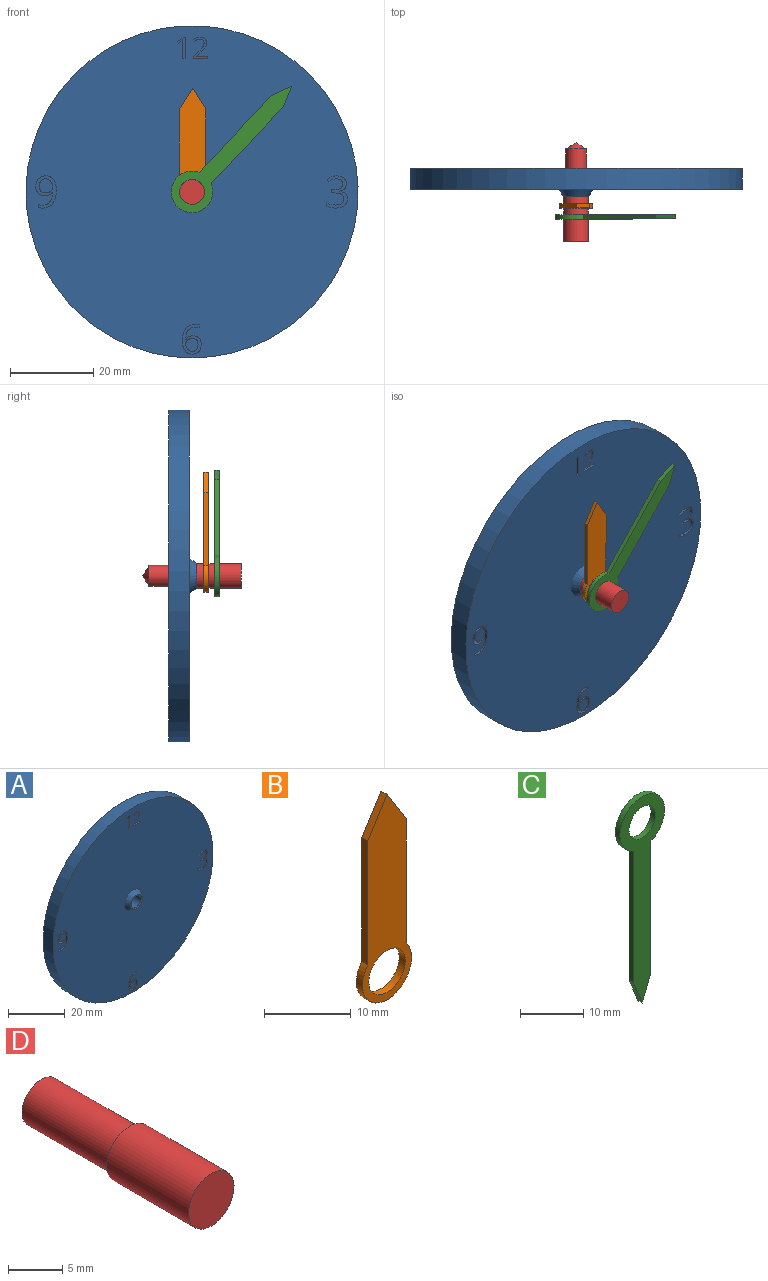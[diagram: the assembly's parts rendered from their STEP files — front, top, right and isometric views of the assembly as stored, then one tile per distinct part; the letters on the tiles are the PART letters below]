
ASSEMBLY  parts=4 mates=4
PART A: 121 faces, bbox 80x6.8x80 mm
  f0: plane 80x80mm, normal (0,-1,0), area 4903.6mm2, adj f1,f2,f6,f7,f8,f9,f10,f11
  f1: cone r=4.25mm half-angle=35.4deg, axis (0,1,0), area 50.1mm2, adj f0,f5
  f2: cylinder r=40mm len=80mm, axis (0,1,0), area 1256.6mm2, adj f0,f3
  f3: plane 80x80mm, normal (0,1,0), area 5006.9mm2, adj f2,f4
  f4: cylinder r=2.5mm len=6.53mm, axis (0,-1,0), area 102.5mm2, adj f3,f5
  f5: cone r=2.5mm half-angle=60deg, axis (0,-1,0), area 9.3mm2, adj f1,f4
  f6: extruded ~2.25x1.5mm, area 3.6mm2, adj f0,f7,f30,f31
  f7: extruded ~1.71x1.5mm, area 2.9mm2, adj f0,f6,f8,f31
  f8: extruded ~1.6x1.5mm, area 2.6mm2, adj f0,f7,f9,f31
  f9: extruded ~1.7x1.5mm, area 2.8mm2, adj f0,f8,f10,f31
  f10: extruded ~1.53x1.5mm, area 2.5mm2, adj f0,f9,f11,f31
  f11: extruded ~1.5x1.47mm, area 2.4mm2, adj f0,f10,f12,f31
  f12: extruded ~1.65x1.5mm, area 2.9mm2, adj f0,f11,f13,f31
  f13: plane 1.5x0.06mm, normal (0,0,-1), area 0.1mm2, adj f0,f12,f14,f31
  f14: extruded ~2.19x1.5mm, area 3.5mm2, adj f0,f13,f15,f31
  f15: extruded ~1.71x1.5mm, area 2.9mm2, adj f0,f14,f16,f31
  f16: extruded ~1.5x0.84mm, area 1.3mm2, adj f0,f15,f17,f31
  f17: plane 1.5x0.68mm, normal (-1,0,0), area 1mm2, adj f0,f16,f18,f31
  f18: extruded ~1.5x0.84mm, area 1.3mm2, adj f0,f17,f19,f31
  f19: extruded ~2.35x1.5mm, area 4mm2, adj f0,f18,f30,f31
  f20: extruded ~1.5x0.8mm, area 1.3mm2, adj f21,f29,f31,f32
  f21: extruded ~1.5x0.67mm, area 1.3mm2, adj f20,f22,f31,f32
  f22: extruded ~1.5x0.91mm, area 1.4mm2, adj f21,f23,f31,f32
  f23: extruded ~1.5x0.64mm, area 1mm2, adj f22,f24,f31,f32
  f24: extruded ~1.5x0.57mm, area 1.1mm2, adj f23,f25,f31,f32
  f25: extruded ~1.5x0.78mm, area 1.2mm2, adj f24,f26,f31,f32
  f26: extruded ~1.5x1.03mm, area 1.7mm2, adj f25,f27,f31,f32
  f27: extruded ~1.5x1.08mm, area 1.7mm2, adj f26,f28,f31,f32
  f28: extruded ~1.5x1.23mm, area 2mm2, adj f27,f29,f31,f32
  f29: extruded ~1.5x1.05mm, area 1.8mm2, adj f20,f28,f31,f32
  f30: extruded ~3.06x1.5mm, area 4.8mm2, adj f0,f6,f19,f31
  f31: plane 7.14x4.53mm, normal (0,-1,0), area 12.5mm2, adj f6,f7,f8,f9,f10,f11,f12,f13
  f32: plane 3.13x2.94mm, normal (0,-1,0), area 7.4mm2, adj f20,f21,f22,f23,f24,f25,f26,f27
  f33: extruded ~1.5x1.38mm, area 2.3mm2, adj f0,f34,f60,f61
  f34: extruded ~1.71x1.5mm, area 2.7mm2, adj f0,f33,f35,f61
  f35: extruded ~1.5x1.28mm, area 1.9mm2, adj f0,f34,f36,f61
  f36: extruded ~1.5x1.07mm, area 1.8mm2, adj f0,f35,f37,f61
  f37: plane 1.5x0.58mm, normal (0.8,0,0.6), area 1.1mm2, adj f0,f36,f38,f61
  f38: extruded ~1.5x1mm, area 1.7mm2, adj f0,f37,f39,f61
  f39: extruded ~1.5x0.93mm, area 1.4mm2, adj f0,f38,f40,f61
  f40: extruded ~1.5x1.03mm, area 1.6mm2, adj f0,f39,f41,f61
  f41: extruded ~1.5x0.87mm, area 1.5mm2, adj f0,f40,f42,f61
  f42: extruded ~1.5x1.08mm, area 1.9mm2, adj f0,f41,f43,f61
  f43: extruded ~1.5x1.4mm, area 2.2mm2, adj f0,f42,f44,f61
  f44: plane 1.5x0.75mm, normal (0,0,-1), area 1.1mm2, adj f0,f43,f45,f61
  f45: plane 1.5x0.74mm, normal (1,0,0), area 1.1mm2, adj f0,f44,f46,f61
  f46: plane 1.5x0.74mm, normal (0,0,1), area 1.1mm2, adj f0,f45,f47,f61
  f47: extruded ~2.15x1.5mm, area 4.3mm2, adj f0,f46,f48,f61
  f48: extruded ~1.95x1.53mm, area 4.3mm2, adj f0,f47,f49,f61
  f49: extruded ~1.5x1.05mm, area 1.6mm2, adj f0,f48,f50,f61
  f50: extruded ~1.5x1.04mm, area 1.7mm2, adj f0,f49,f51,f61
  f51: plane 1.5x0.81mm, normal (1,0,0), area 1.2mm2, adj f0,f50,f52,f61
  f52: extruded ~1.5x0.97mm, area 1.5mm2, adj f0,f51,f53,f61
  f53: extruded ~1.5x1.1mm, area 1.7mm2, adj f0,f52,f54,f61
  f54: extruded ~2.12x1.5mm, area 3.4mm2, adj f0,f53,f55,f61
  f55: extruded ~1.66x1.5mm, area 2.8mm2, adj f0,f54,f56,f61
  f56: extruded ~1.5x1.22mm, area 2mm2, adj f0,f55,f57,f61
  f57: extruded ~1.5x1.35mm, area 2.2mm2, adj f0,f56,f58,f61
  f58: plane 1.5x0.04mm, normal (-1,0,0), area 0.1mm2, adj f0,f57,f59,f61
  f59: extruded ~1.5x1.15mm, area 2mm2, adj f0,f58,f60,f61
  f60: extruded ~1.5x1.18mm, area 1.9mm2, adj f0,f33,f59,f61
  f61: plane 7.75x4.93mm, normal (0,-1,0), area 13.2mm2, adj f33,f34,f35,f36,f37,f38,f39,f40
  f62: plane 1.5x0.55mm, normal (-1,0,0), area 0.8mm2, adj f0,f63,f81,f82
  f63: plane 2.67x1.5mm, normal (0,0,-1), area 4mm2, adj f0,f62,f64,f82
  f64: plane 1.5x0.03mm, normal (-1,0,0), area 0mm2, adj f0,f63,f65,f82
  f65: plane 1.5x1.14mm, normal (-0.7,0,0.71), area 2.4mm2, adj f0,f64,f66,f82
  f66: extruded ~1.5x1.22mm, area 2.4mm2, adj f0,f65,f67,f82
  f67: extruded ~1.5x0.98mm, area 1.5mm2, adj f0,f66,f68,f82
  f68: extruded ~1.5x1.01mm, area 1.7mm2, adj f0,f67,f69,f82
  f69: extruded ~1.5x1.15mm, area 1.9mm2, adj f0,f68,f70,f82
  f70: extruded ~1.56x1.5mm, area 2.6mm2, adj f0,f69,f71,f82
  f71: plane 1.5x0.4mm, normal (0.79,0,0.61), area 0.8mm2, adj f0,f70,f72,f82
  f72: extruded ~1.5x0.64mm, area 1.1mm2, adj f0,f71,f73,f82
  f73: extruded ~1.5x0.61mm, area 0.9mm2, adj f0,f72,f74,f82
  f74: extruded ~1.5x0.7mm, area 1.1mm2, adj f0,f73,f75,f82
  f75: extruded ~1.5x0.66mm, area 1.1mm2, adj f0,f74,f76,f82
  f76: extruded ~1.5x0.55mm, area 0.8mm2, adj f0,f75,f77,f82
  f77: extruded ~1.5x0.53mm, area 0.9mm2, adj f0,f76,f78,f82
  f78: extruded ~1.5x0.9mm, area 1.8mm2, adj f0,f77,f79,f82
  f79: plane 1.5x1.37mm, normal (0.71,0,-0.71), area 2.9mm2, adj f0,f78,f80,f82
  f80: plane 1.5x0.51mm, normal (1,0,0), area 0.8mm2, adj f0,f79,f81,f82
  f81: plane 3.41x1.5mm, normal (0,0,1), area 5.1mm2, adj f0,f62,f80,f82
  f82: plane 5.27x3.41mm, normal (0,-1,0), area 5.9mm2, adj f62,f63,f64,f65,f66,f67,f68,f69
  f83: plane 5.19x1.5mm, normal (-1,0,0), area 7.8mm2, adj f0,f84,f91,f92
  f84: plane 1.5x0.5mm, normal (0,0,-1), area 0.7mm2, adj f0,f83,f85,f92
  f85: plane 1.5x1.37mm, normal (0.61,0,-0.79), area 2.6mm2, adj f0,f84,f86,f92
  f86: plane 1.5x0.4mm, normal (0.79,0,0.61), area 0.8mm2, adj f0,f85,f87,f92
  f87: extruded ~1.5x0.85mm, area 1.6mm2, adj f0,f86,f88,f92
  f88: extruded ~1.5x0.17mm, area 0.3mm2, adj f0,f87,f89,f92
  f89: extruded ~1.5x0.87mm, area 1.3mm2, adj f0,f88,f90,f92
  f90: plane 3.7x1.5mm, normal (1,0,0), area 5.6mm2, adj f0,f89,f91,f92
  f91: plane 1.5x0.58mm, normal (0,0,1), area 0.9mm2, adj f0,f83,f90,f92
  f92: plane 5.19x1.87mm, normal (0,-1,0), area 3.7mm2, adj f83,f84,f85,f86,f87,f88,f89,f90
  f93: extruded ~1.78x1.5mm, area 2.7mm2, adj f0,f94,f118,f119
  f94: extruded ~1.5x1.15mm, area 2.2mm2, adj f0,f93,f95,f119
  f95: extruded ~1.5x1.34mm, area 2.1mm2, adj f0,f94,f96,f119
  f96: extruded ~1.73x1.5mm, area 2.9mm2, adj f0,f95,f97,f119
  f97: extruded ~1.85x1.5mm, area 3mm2, adj f0,f96,f98,f119
  f98: extruded ~1.67x1.5mm, area 2.7mm2, adj f0,f97,f99,f119
  f99: extruded ~1.59x1.5mm, area 2.6mm2, adj f0,f98,f100,f119
  f100: extruded ~1.5x1.06mm, area 1.6mm2, adj f0,f99,f101,f119
  f101: extruded ~1.5x0.75mm, area 1.5mm2, adj f0,f100,f102,f119
  f102: plane 1.5x0.06mm, normal (0,0,1), area 0.1mm2, adj f0,f101,f103,f119
  f103: extruded ~2.35x1.5mm, area 3.7mm2, adj f0,f102,f104,f119
  f104: extruded ~1.87x1.5mm, area 3.1mm2, adj f0,f103,f105,f119
  f105: extruded ~1.5x0.94mm, area 1.4mm2, adj f0,f104,f106,f119
  f106: plane 1.5x0.74mm, normal (1,0,0), area 1.1mm2, adj f0,f105,f107,f119
  f107: extruded ~1.5x0.95mm, area 1.4mm2, adj f0,f106,f118,f119
  f108: extruded ~1.5x0.87mm, area 1.4mm2, adj f109,f117,f119,f120
  f109: extruded ~1.5x0.72mm, area 1.4mm2, adj f108,f110,f119,f120
  f110: extruded ~1.5x1mm, area 1.5mm2, adj f109,f111,f119,f120
  f111: extruded ~1.5x0.69mm, area 1.1mm2, adj f110,f112,f119,f120
  f112: extruded ~1.5x0.62mm, area 1.2mm2, adj f111,f113,f119,f120
  f113: extruded ~1.5x0.86mm, area 1.3mm2, adj f112,f114,f119,f120
  f114: extruded ~1.5x1.13mm, area 1.9mm2, adj f113,f115,f119,f120
  f115: extruded ~1.5x1.17mm, area 1.9mm2, adj f114,f116,f119,f120
  f116: extruded ~1.5x1.32mm, area 2.1mm2, adj f115,f117,f119,f120
  f117: extruded ~1.5x1.14mm, area 1.9mm2, adj f108,f116,f119,f120
  f118: extruded ~4.42x3.42mm, area 9.6mm2, adj f0,f93,f107,f119
  f119: plane 7.75x4.92mm, normal (0,-1,0), area 14.7mm2, adj f93,f94,f95,f96,f97,f98,f99,f100
  f120: plane 3.39x3.21mm, normal (0,-1,0), area 8.8mm2, adj f108,f109,f110,f111,f112,f113,f114,f115
PART B: 8 faces, bbox 8x1x29 mm
  f0: plane 17.5x1mm, normal (-1,0,0), area 17.5mm2, adj f1,f4,f5,f6
  f1: cylinder r=4mm len=8mm, axis (0,1,0), area 18mm2, adj f0,f2,f5,f6
  f2: plane 17.5x1mm, normal (1,0,0), area 17.5mm2, adj f1,f3,f5,f6
  f3: plane 5x3.12mm, normal (0.85,0,0.53), area 5.9mm2, adj f2,f4,f5,f6
  f4: plane 5x3.12mm, normal (-0.85,0,0.53), area 5.9mm2, adj f0,f3,f5,f6
  f5: plane 29x8mm, normal (0,-1,0), area 140.9mm2, adj f0,f1,f2,f3,f4,f7
  f6: plane 29x8mm, normal (0,1,0), area 140.9mm2, adj f0,f1,f2,f3,f4,f7
  f7: cylinder r=2.97mm len=5.94mm, axis (0,1,0), area 18.7mm2, adj f5,f6
PART C: 8 faces, bbox 10x1x40 mm
  f0: plane 25.4x1mm, normal (1,0,0), area 25.4mm2, adj f1,f4,f5,f6
  f1: cylinder r=5mm len=10mm, axis (0,1,0), area 27.4mm2, adj f0,f2,f5,f6
  f2: plane 25.4x1mm, normal (-1,0,0), area 25.4mm2, adj f1,f3,f5,f6
  f3: plane 5x1.96mm, normal (-0.93,0,-0.36), area 5.4mm2, adj f2,f4,f5,f6
  f4: plane 5x1.96mm, normal (0.93,0,-0.36), area 5.4mm2, adj f0,f3,f5,f6
  f5: plane 40x10mm, normal (0,-1,0), area 159.1mm2, adj f0,f1,f2,f3,f4,f7
  f6: plane 40x10mm, normal (0,1,0), area 159.1mm2, adj f0,f1,f2,f3,f4,f7
  f7: cylinder r=2.97mm len=5.94mm, axis (0,1,0), area 18.7mm2, adj f5,f6
PART D: 5 faces, bbox 5.9x23.8x5.9 mm
  f0: cylinder r=2.97mm len=10.7mm, axis (0,1,0), area 199.7mm2, adj f1,f3
  f1: plane 5.94x5.94mm, normal (0,-1,0), area 27.7mm2, adj f0
  f2: cylinder r=2.5mm len=11.28mm, axis (0,-1,0), area 177.2mm2, adj f3,f4
  f3: cone r=2.5mm half-angle=60deg, axis (0,-1,0), area 9.3mm2, adj f0,f2
  f4: cone r=0mm half-angle=59deg, axis (0,-1,0), area 22.9mm2, adj f2
PLACE A at identity fixed
PLACE B rot(axis=(0,1,0),0.5deg) t=(0,1,0)mm
PLACE C rot(axis=(0,-1,0),136.7deg) t=(0,2.35,0)mm
PLACE D at identity
MATE planar C.f7 <-> D.f0  axis (0,-1,0) through (0,-24.65,0)mm
MATE fastened A.f1 <-> D.f0  axis (0,-1,0) through (0,-19.03,0)mm
MATE revolute D.f0 <-> B.f7  axis (0,-1,0) through (0,-30,0)mm
MATE cylindrical D.f0 <-> C.f7  axis (0,-1,0) through (0,-30,0)mm
